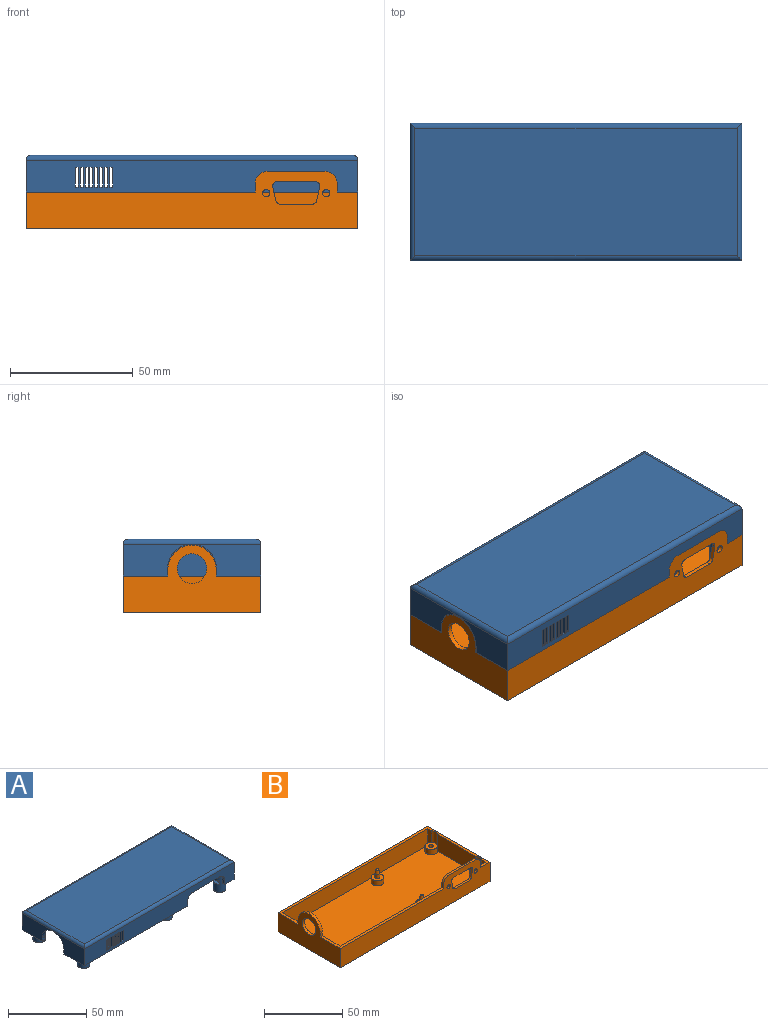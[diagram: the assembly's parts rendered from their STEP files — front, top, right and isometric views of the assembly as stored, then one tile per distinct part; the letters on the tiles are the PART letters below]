
ASSEMBLY  parts=2 mates=1
PART A: 142 faces, bbox 135x56x24 mm
  f0: cylinder r=4mm len=20mm, axis (0,0,1), area 486.2mm2, adj f21,f38,f122,f123,f124,f125
  f1: cylinder r=4mm len=20mm, axis (0,0,1), area 486.2mm2, adj f21,f39,f128,f129,f130,f131
  f2: cylinder r=1.55mm len=4.4mm, axis (0,0,-1), area 42.9mm2, adj f39,f130
  f3: cylinder r=1.55mm len=4.4mm, axis (0,0,-1), area 42.9mm2, adj f38,f124
  f4: cylinder r=4mm len=22mm, axis (0,0,1), area 461.3mm2, adj f9,f10,f15,f21,f108,f110,f111,f112
  f5: cylinder r=4mm len=22mm, axis (0,0,1), area 461.3mm2, adj f8,f9,f15,f21,f109,f116,f117,f118
  f6: cylinder r=1.6mm len=6.4mm, axis (0,0,1), area 64.3mm2, adj f109,f118
  f7: cylinder r=1.6mm len=6.4mm, axis (0,0,1), area 64.3mm2, adj f108,f112
  f8: plane 13x3.35mm, normal (-1,0,0), area 43.6mm2, adj f5,f14,f15,f21
  f9: plane 34.71x13mm, normal (-1,0,0), area 451.2mm2, adj f4,f5,f15,f21
  f10: plane 13x3.35mm, normal (-1,0,0), area 43.6mm2, adj f4,f11,f15,f21
  f11: plane 131x13mm, normal (0,1,0), area 1356.4mm2, adj f10,f15,f17,f20,f21,f25,f26,f27
  f12: plane 135x13mm, normal (0,1,0), area 1678.2mm2, adj f15,f16,f18,f30,f44,f45,f46,f47
  f13: plane 135x13mm, normal (0,-1,0), area 1408.4mm2, adj f15,f16,f17,f18,f25,f26,f27,f28
  f14: plane 131x13mm, normal (0,-1,0), area 1626.2mm2, adj f8,f15,f20,f21,f44,f45,f46,f47
  f15: plane 135x56mm, normal (0,0,-1), area 415.9mm2, adj f4,f5,f8,f9,f10,f11,f12,f13
  f16: plane 56x13mm, normal (-1,0,0), area 522.3mm2, adj f12,f13,f15,f17,f22,f23,f24,f31
  f17: plane 93.2x18.2mm, normal (0,0,-1), area 218.8mm2, adj f11,f13,f16,f20,f24,f25
  f18: plane 56x13mm, normal (1,0,0), area 728mm2, adj f12,f13,f15,f32
  f19: plane 131x52mm, normal (0,0,1), area 6812mm2, adj f30,f31,f32,f33
  f20: plane 52x13mm, normal (1,0,0), area 470.3mm2, adj f11,f14,f15,f17,f21,f22,f23,f24
  f21: plane 131x52mm, normal (0,0,-1), area 6517.7mm2, adj f0,f1,f4,f5,f8,f9,f10,f11
  f22: cylinder r=9.8mm len=19.6mm, axis (-1,0,0), area 61.6mm2, adj f16,f20,f23,f24
  f23: plane 2.8x2mm, normal (0,-1,0), area 5.6mm2, adj f15,f16,f20,f22
  f24: plane 2.8x2mm, normal (0,1,0), area 5.6mm2, adj f16,f17,f20,f22
  f25: plane 3.4x2mm, normal (1,0,0), area 6.8mm2, adj f11,f13,f17,f29
  f26: plane 3.4x2mm, normal (-1,0,0), area 6.8mm2, adj f11,f13,f15,f27
  f27: cylinder r=5mm len=5mm, axis (0,-1,0), area 15.7mm2, adj f11,f13,f26,f28
  f28: plane 23.4x2mm, normal (0,0,-1), area 46.8mm2, adj f11,f13,f27,f29
  f29: cylinder r=5mm len=5mm, axis (0,-1,0), area 15.7mm2, adj f11,f13,f25,f28
  f30: cylinder r=2mm len=135mm, axis (1,0,0), area 419.5mm2, adj f12,f19,f31,f32
  f31: cylinder r=2mm len=56mm, axis (0,1,0), area 171.4mm2, adj f16,f19,f30,f33
  f32: cylinder r=2mm len=56mm, axis (0,-1,0), area 171.4mm2, adj f18,f19,f30,f33
  f33: cylinder r=2mm len=135mm, axis (-1,0,0), area 419.5mm2, adj f13,f19,f31,f32
  f34: cylinder r=4mm len=20mm, axis (0,0,1), area 502.7mm2, adj f21,f35
  f35: plane 8x8mm, normal (0,0,-1), area 42.2mm2, adj f34,f42
  f36: cylinder r=4mm len=20mm, axis (0,0,1), area 502.7mm2, adj f21,f37
  f37: plane 8x8mm, normal (0,0,-1), area 42.2mm2, adj f36,f40
  f38: plane 8x8mm, normal (0,0,-1), area 42.7mm2, adj f0,f3
  f39: plane 8x8mm, normal (0,0,-1), area 42.7mm2, adj f1,f2
  f40: cylinder r=1.6mm len=15mm, axis (0,0,-1), area 150.8mm2, adj f37,f41
  f41: plane 3.2x3.2mm, normal (0,0,-1), area 8mm2, adj f40
  f42: cylinder r=1.6mm len=15mm, axis (0,0,-1), area 150.8mm2, adj f35,f43
  f43: plane 3.2x3.2mm, normal (0,0,-1), area 8mm2, adj f42
  f44: plane 2x1.2mm, normal (0,0,-1), area 2.4mm2, adj f12,f14,f45,f47
  f45: plane 8x2mm, normal (1,0,0), area 16mm2, adj f12,f14,f44,f46
  f46: plane 2x1.2mm, normal (0,0,1), area 2.4mm2, adj f12,f14,f45,f47
  f47: plane 8x2mm, normal (-1,0,0), area 16mm2, adj f12,f14,f44,f46
  f48: plane 2x1.2mm, normal (0,0,-1), area 2.4mm2, adj f12,f14,f49,f51
  f49: plane 8x2mm, normal (1,0,0), area 16mm2, adj f12,f14,f48,f50
  f50: plane 2x1.2mm, normal (0,0,1), area 2.4mm2, adj f12,f14,f49,f51
  f51: plane 8x2mm, normal (-1,0,0), area 16mm2, adj f12,f14,f48,f50
  f52: plane 2x1.2mm, normal (0,0,-1), area 2.4mm2, adj f12,f14,f53,f55
  f53: plane 8x2mm, normal (1,0,0), area 16mm2, adj f12,f14,f52,f54
  f54: plane 2x1.2mm, normal (0,0,1), area 2.4mm2, adj f12,f14,f53,f55
  f55: plane 8x2mm, normal (-1,0,0), area 16mm2, adj f12,f14,f52,f54
  f56: plane 2x1.2mm, normal (0,0,-1), area 2.4mm2, adj f12,f14,f57,f59
  f57: plane 8x2mm, normal (1,0,0), area 16mm2, adj f12,f14,f56,f58
  f58: plane 2x1.2mm, normal (0,0,1), area 2.4mm2, adj f12,f14,f57,f59
  f59: plane 8x2mm, normal (-1,0,0), area 16mm2, adj f12,f14,f56,f58
  f60: plane 2x1.2mm, normal (0,0,-1), area 2.4mm2, adj f12,f14,f61,f63
  f61: plane 8x2mm, normal (1,0,0), area 16mm2, adj f12,f14,f60,f62
  f62: plane 2x1.2mm, normal (0,0,1), area 2.4mm2, adj f12,f14,f61,f63
  f63: plane 8x2mm, normal (-1,0,0), area 16mm2, adj f12,f14,f60,f62
  f64: plane 2x1.2mm, normal (0,0,-1), area 2.4mm2, adj f12,f14,f65,f67
  f65: plane 8x2mm, normal (1,0,0), area 16mm2, adj f12,f14,f64,f66
  f66: plane 2x1.2mm, normal (0,0,1), area 2.4mm2, adj f12,f14,f65,f67
  f67: plane 8x2mm, normal (-1,0,0), area 16mm2, adj f12,f14,f64,f66
  f68: plane 2x1.2mm, normal (0,0,-1), area 2.4mm2, adj f12,f14,f69,f71
  f69: plane 8x2mm, normal (1,0,0), area 16mm2, adj f12,f14,f68,f70
  f70: plane 2x1.2mm, normal (0,0,1), area 2.4mm2, adj f12,f14,f69,f71
  f71: plane 8x2mm, normal (-1,0,0), area 16mm2, adj f12,f14,f68,f70
  f72: plane 8x2mm, normal (1,0,0), area 16mm2, adj f12,f14,f73,f75
  f73: plane 2x1.2mm, normal (0,0,1), area 2.4mm2, adj f12,f14,f72,f74
  f74: plane 8x2mm, normal (-1,0,0), area 16mm2, adj f12,f14,f73,f75
  f75: plane 2x1.2mm, normal (0,0,-1), area 2.4mm2, adj f12,f14,f72,f74
  f76: plane 8x2mm, normal (-1,0,0), area 16mm2, adj f11,f13,f77,f79
  f77: plane 2x1.2mm, normal (0,0,1), area 2.4mm2, adj f11,f13,f76,f78
  f78: plane 8x2mm, normal (1,0,0), area 16mm2, adj f11,f13,f77,f79
  f79: plane 2x1.2mm, normal (0,0,-1), area 2.4mm2, adj f11,f13,f76,f78
  f80: plane 8x2mm, normal (-1,0,0), area 16mm2, adj f11,f13,f81,f83
  f81: plane 2x1.2mm, normal (0,0,1), area 2.4mm2, adj f11,f13,f80,f82
  f82: plane 8x2mm, normal (1,0,0), area 16mm2, adj f11,f13,f81,f83
  f83: plane 2x1.2mm, normal (0,0,-1), area 2.4mm2, adj f11,f13,f80,f82
  f84: plane 8x2mm, normal (-1,0,0), area 16mm2, adj f11,f13,f85,f87
  f85: plane 2x1.2mm, normal (0,0,1), area 2.4mm2, adj f11,f13,f84,f86
  f86: plane 8x2mm, normal (1,0,0), area 16mm2, adj f11,f13,f85,f87
  f87: plane 2x1.2mm, normal (0,0,-1), area 2.4mm2, adj f11,f13,f84,f86
  f88: plane 8x2mm, normal (-1,0,0), area 16mm2, adj f11,f13,f89,f91
  f89: plane 2x1.2mm, normal (0,0,1), area 2.4mm2, adj f11,f13,f88,f90
  f90: plane 8x2mm, normal (1,0,0), area 16mm2, adj f11,f13,f89,f91
  f91: plane 2x1.2mm, normal (0,0,-1), area 2.4mm2, adj f11,f13,f88,f90
  f92: plane 8x2mm, normal (-1,0,0), area 16mm2, adj f11,f13,f93,f95
  f93: plane 2x1.2mm, normal (0,0,1), area 2.4mm2, adj f11,f13,f92,f94
  f94: plane 8x2mm, normal (1,0,0), area 16mm2, adj f11,f13,f93,f95
  f95: plane 2x1.2mm, normal (0,0,-1), area 2.4mm2, adj f11,f13,f92,f94
  f96: plane 8x2mm, normal (-1,0,0), area 16mm2, adj f11,f13,f97,f99
  f97: plane 2x1.2mm, normal (0,0,1), area 2.4mm2, adj f11,f13,f96,f98
  f98: plane 8x2mm, normal (1,0,0), area 16mm2, adj f11,f13,f97,f99
  f99: plane 2x1.2mm, normal (0,0,-1), area 2.4mm2, adj f11,f13,f96,f98
  f100: plane 8x2mm, normal (-1,0,0), area 16mm2, adj f11,f13,f101,f103
  f101: plane 2x1.2mm, normal (0,0,1), area 2.4mm2, adj f11,f13,f100,f102
  f102: plane 8x2mm, normal (1,0,0), area 16mm2, adj f11,f13,f101,f103
  f103: plane 2x1.2mm, normal (0,0,-1), area 2.4mm2, adj f11,f13,f100,f102
  f104: plane 2x1.2mm, normal (0,0,-1), area 2.4mm2, adj f11,f13,f105,f107
  f105: plane 8x2mm, normal (-1,0,0), area 16mm2, adj f11,f13,f104,f106
  f106: plane 2x1.2mm, normal (0,0,1), area 2.4mm2, adj f11,f13,f105,f107
  f107: plane 8x2mm, normal (1,0,0), area 16mm2, adj f11,f13,f104,f106
  f108: plane 8x8mm, normal (0,0,-1), area 42.2mm2, adj f4,f7
  f109: plane 8x8mm, normal (0,0,-1), area 42.2mm2, adj f5,f6
  f110: plane 4.45x2.6mm, normal (0,-1,0), area 11.6mm2, adj f4,f112,f113,f115
  f111: plane 4.45x2.6mm, normal (0,1,0), area 11.6mm2, adj f4,f112,f113,f114
  f112: plane 7.29x5.7mm, normal (0,0,1), area 26.7mm2, adj f4,f7,f110,f111,f114,f115
  f113: plane 7.29x5.7mm, normal (0,0,-1), area 26.7mm2, adj f4,f110,f111,f114,f115,f135
  f114: plane 2.85x2.6mm, normal (-0.87,0.5,0), area 8.6mm2, adj f111,f112,f113,f115
  f115: plane 2.85x2.6mm, normal (-0.87,-0.5,0), area 8.6mm2, adj f110,f112,f113,f114
  f116: plane 4.45x2.6mm, normal (0,-1,0), area 11.6mm2, adj f5,f118,f119,f121
  f117: plane 4.45x2.6mm, normal (0,1,0), area 11.6mm2, adj f5,f118,f119,f120
  f118: plane 7.29x5.7mm, normal (0,0,1), area 26.7mm2, adj f5,f6,f116,f117,f120,f121
  f119: plane 7.29x5.7mm, normal (0,0,-1), area 26.7mm2, adj f5,f116,f117,f120,f121,f137
  f120: plane 2.85x2.6mm, normal (-0.87,0.5,0), area 8.6mm2, adj f117,f118,f119,f121
  f121: plane 2.85x2.6mm, normal (-0.87,-0.5,0), area 8.6mm2, adj f116,f118,f119,f120
  f122: plane 4.45x2.6mm, normal (0,-1,0), area 11.6mm2, adj f0,f124,f125,f127
  f123: plane 4.45x2.6mm, normal (0,1,0), area 11.6mm2, adj f0,f124,f125,f126
  f124: plane 7.29x5.7mm, normal (0,0,1), area 27.2mm2, adj f0,f3,f122,f123,f126,f127
  f125: plane 7.29x5.7mm, normal (0,0,-1), area 27.2mm2, adj f0,f122,f123,f126,f127,f139
  f126: plane 2.85x2.6mm, normal (-0.87,0.5,0), area 8.6mm2, adj f123,f124,f125,f127
  f127: plane 2.85x2.6mm, normal (-0.87,-0.5,0), area 8.6mm2, adj f122,f124,f125,f126
  f128: plane 4.45x2.6mm, normal (0,-1,0), area 11.6mm2, adj f1,f130,f131,f133
  f129: plane 4.45x2.6mm, normal (0,1,0), area 11.6mm2, adj f1,f130,f131,f132
  f130: plane 7.29x5.7mm, normal (0,0,1), area 27.2mm2, adj f1,f2,f128,f129,f132,f133
  f131: plane 7.29x5.7mm, normal (0,0,-1), area 27.2mm2, adj f1,f128,f129,f132,f133,f141
  f132: plane 2.85x2.6mm, normal (-0.87,0.5,0), area 8.6mm2, adj f129,f130,f131,f133
  f133: plane 2.85x2.6mm, normal (-0.87,-0.5,0), area 8.6mm2, adj f128,f130,f131,f132
  f134: plane 3.2x3.2mm, normal (0,0,-1), area 8mm2, adj f135
  f135: cylinder r=1.6mm len=13mm, axis (0,0,1), area 130.7mm2, adj f113,f134
  f136: plane 3.2x3.2mm, normal (0,0,-1), area 8mm2, adj f137
  f137: cylinder r=1.6mm len=13mm, axis (0,0,1), area 130.7mm2, adj f119,f136
  f138: plane 3.1x3.1mm, normal (0,0,-1), area 7.5mm2, adj f139
  f139: cylinder r=1.55mm len=8mm, axis (0,0,-1), area 77.9mm2, adj f125,f138
  f140: plane 3.1x3.1mm, normal (0,0,-1), area 7.5mm2, adj f141
  f141: cylinder r=1.55mm len=8mm, axis (0,0,-1), area 77.9mm2, adj f131,f140
PART B: 71 faces, bbox 135x56x28 mm
  f0: plane 34.71x13mm, normal (-1,0,0), area 451.2mm2, adj f7,f31,f55,f57,f67,f68
  f1: plane 13x3.35mm, normal (-1,0,0), area 43.6mm2, adj f7,f31,f37,f57,f68
  f2: plane 13x3.35mm, normal (-1,0,0), area 43.6mm2, adj f7,f31,f38,f55,f67
  f3: cylinder r=1.55mm len=3.1mm, axis (0,0,-1), area 19.5mm2, adj f58,f65
  f4: cylinder r=1.55mm len=3.1mm, axis (0,0,-1), area 19.5mm2, adj f56,f63
  f5: cylinder r=1.55mm len=3.1mm, axis (0,0,-1), area 19.5mm2, adj f50,f61
  f6: cylinder r=1.55mm len=3.1mm, axis (0,0,-1), area 19.5mm2, adj f48,f59
  f7: plane 131x52mm, normal (0,0,1), area 6517.7mm2, adj f0,f1,f2,f36,f37,f38,f39,f43
  f8: plane 3.4x1.5mm, normal (1,0,0), area 5.1mm2, adj f10,f23,f24,f31
  f9: plane 3.4x1.5mm, normal (-1,0,0), area 5.1mm2, adj f12,f23,f24,f30
  f10: cylinder r=5mm len=5mm, axis (0,-1,0), area 11.8mm2, adj f8,f11,f23,f24
  f11: plane 23.4x1.5mm, normal (0,0,1), area 35.1mm2, adj f10,f12,f23,f24
  f12: cylinder r=5mm len=5mm, axis (0,-1,0), area 11.8mm2, adj f9,f11,f23,f24
  f13: cylinder r=2mm len=1.96mm, axis (0,-1,0), area 4.1mm2, adj f14,f21,f23,f24
  f14: plane 5.4x1.5mm, normal (0.98,0,0.21), area 8.3mm2, adj f13,f15,f23,f24
  f15: cylinder r=2mm len=2.42mm, axis (0,-1,0), area 5.3mm2, adj f14,f16,f23,f24
  f16: plane 15.06x1.5mm, normal (0,0,-1), area 22.6mm2, adj f15,f17,f23,f24
  f17: cylinder r=2mm len=2.42mm, axis (0,-1,0), area 5.3mm2, adj f16,f18,f23,f24
  f18: plane 5.4x1.5mm, normal (-0.98,0,0.21), area 8.3mm2, adj f17,f19,f23,f24
  f19: cylinder r=2mm len=1.96mm, axis (0,-1,0), area 4.1mm2, adj f18,f21,f23,f24
  f20: cylinder r=1.5mm len=3mm, axis (0,-1,0), area 14.1mm2, adj f23,f24
  f21: plane 12.76x1.5mm, normal (0,0,1), area 19.1mm2, adj f13,f19,f23,f24
  f22: cylinder r=1.5mm len=3mm, axis (0,-1,0), area 14.1mm2, adj f23,f24
  f23: plane 33.4x17.4mm, normal (0,1,0), area 380.2mm2, adj f8,f9,f10,f11,f12,f13,f14,f15
  f24: plane 135x23.4mm, normal (0,-1,0), area 2115.3mm2, adj f8,f9,f10,f11,f12,f13,f14,f15
  f25: plane 4x0.5mm, normal (-1,0,0), area 2mm2, adj f23,f29,f31,f37
  f26: plane 4x0.5mm, normal (1,0,0), area 2mm2, adj f23,f28,f30,f37
  f27: plane 23.4x0.5mm, normal (0,0,1), area 11.7mm2, adj f23,f28,f29,f37
  f28: cylinder r=5mm len=5mm, axis (0,-1,0), area 3.9mm2, adj f23,f26,f27,f37
  f29: cylinder r=5mm len=5mm, axis (0,-1,0), area 3.9mm2, adj f23,f25,f27,f37
  f30: plane 93.2x18mm, normal (0,0,1), area 218.4mm2, adj f9,f24,f26,f32,f36,f37,f52
  f31: plane 135x56mm, normal (0,0,1), area 415.5mm2, adj f0,f1,f2,f8,f24,f25,f32,f33
  f32: plane 56x28mm, normal (-1,0,0), area 944mm2, adj f24,f30,f31,f34,f35,f51,f52,f53
  f33: plane 56x15mm, normal (1,0,0), area 840mm2, adj f24,f31,f34,f35
  f34: plane 135x15mm, normal (0,1,0), area 2025mm2, adj f31,f32,f33,f35
  f35: plane 135x56mm, normal (0,0,-1), area 7457.9mm2, adj f24,f32,f33,f34,f60,f62,f64,f66
  f36: plane 52x26mm, normal (1,0,0), area 780mm2, adj f7,f30,f31,f37,f38,f51,f52,f53
  f37: plane 131x13mm, normal (0,1,0), area 1413.1mm2, adj f1,f7,f25,f26,f27,f28,f29,f30
  f38: plane 131x13mm, normal (0,-1,0), area 1703mm2, adj f2,f7,f31,f36
  f39: cylinder r=4mm len=8mm, axis (0,0,-1), area 100.5mm2, adj f7,f40
  f40: plane 8x8mm, normal (0,0,1), area 43.2mm2, adj f39,f42
  f41: plane 2x2mm, normal (0,0,1), area 3.1mm2, adj f70
  f42: cylinder r=1.5mm len=3.16mm, axis (0,0,-1), area 29.8mm2, adj f40,f70
  f43: cylinder r=4mm len=8mm, axis (0,0,-1), area 100.5mm2, adj f7,f44
  f44: plane 8x8mm, normal (0,0,1), area 43.2mm2, adj f43,f46
  f45: plane 2x2mm, normal (0,0,1), area 3.1mm2, adj f69
  f46: cylinder r=1.5mm len=3.16mm, axis (0,0,-1), area 29.8mm2, adj f44,f69
  f47: cylinder r=4mm len=8mm, axis (0,0,-1), area 100.5mm2, adj f7,f48
  f48: plane 8x8mm, normal (0,0,1), area 42.7mm2, adj f6,f47
  f49: cylinder r=4mm len=8mm, axis (0,0,-1), area 100.5mm2, adj f7,f50
  f50: plane 8x8mm, normal (0,0,1), area 42.7mm2, adj f5,f49
  f51: cylinder r=6mm len=12mm, axis (-1,0,0), area 75.4mm2, adj f32,f36
  f52: plane 3x2mm, normal (0,-1,0), area 6mm2, adj f30,f32,f36,f53
  f53: cylinder r=10mm len=20mm, axis (-1,0,0), area 62.8mm2, adj f32,f36,f52,f54
  f54: plane 3x2mm, normal (0,1,0), area 6mm2, adj f31,f32,f36,f53
  f55: cylinder r=4mm len=8mm, axis (0,0,-1), area 77.4mm2, adj f0,f2,f7,f56
  f56: plane 8x8mm, normal (0,0,1), area 42.7mm2, adj f4,f55,f67
  f57: cylinder r=4mm len=8mm, axis (0,0,-1), area 77.4mm2, adj f0,f1,f7,f58
  f58: plane 8x8mm, normal (0,0,1), area 42.7mm2, adj f3,f57,f68
  f59: plane 5.7x5.7mm, normal (0,0,-1), area 18mm2, adj f6,f60
  f60: cylinder r=2.85mm len=5.7mm, axis (0,0,-1), area 71.6mm2, adj f35,f59
  f61: plane 5.7x5.7mm, normal (0,0,-1), area 18mm2, adj f5,f62
  f62: cylinder r=2.85mm len=5.7mm, axis (0,0,-1), area 71.6mm2, adj f35,f61
  f63: plane 5.7x5.7mm, normal (0,0,-1), area 18mm2, adj f4,f64
  f64: cylinder r=2.85mm len=5.7mm, axis (0,0,-1), area 71.6mm2, adj f35,f63
  f65: plane 5.7x5.7mm, normal (0,0,-1), area 18mm2, adj f3,f66
  f66: cylinder r=2.85mm len=5.7mm, axis (0,0,-1), area 71.6mm2, adj f35,f65
  f67: cylinder r=4mm len=9mm, axis (0,0,-1), area 52mm2, adj f0,f2,f31,f56
  f68: cylinder r=4mm len=9mm, axis (0,0,-1), area 52mm2, adj f0,f1,f31,f58
  f69: cone r=1mm half-angle=10deg, axis (0,0,-1), area 22.6mm2, adj f45,f46
  f70: cone r=1mm half-angle=10deg, axis (0,0,-1), area 22.6mm2, adj f41,f42
PLACE A t=(-7.49,15.71,-72.24)mm
PLACE B t=(-7.49,15.71,-37.24)mm
MATE cylindrical A.f36 <-> B.f43  axis (0,0,1) through (74.01,23.71,-29.24)mm
